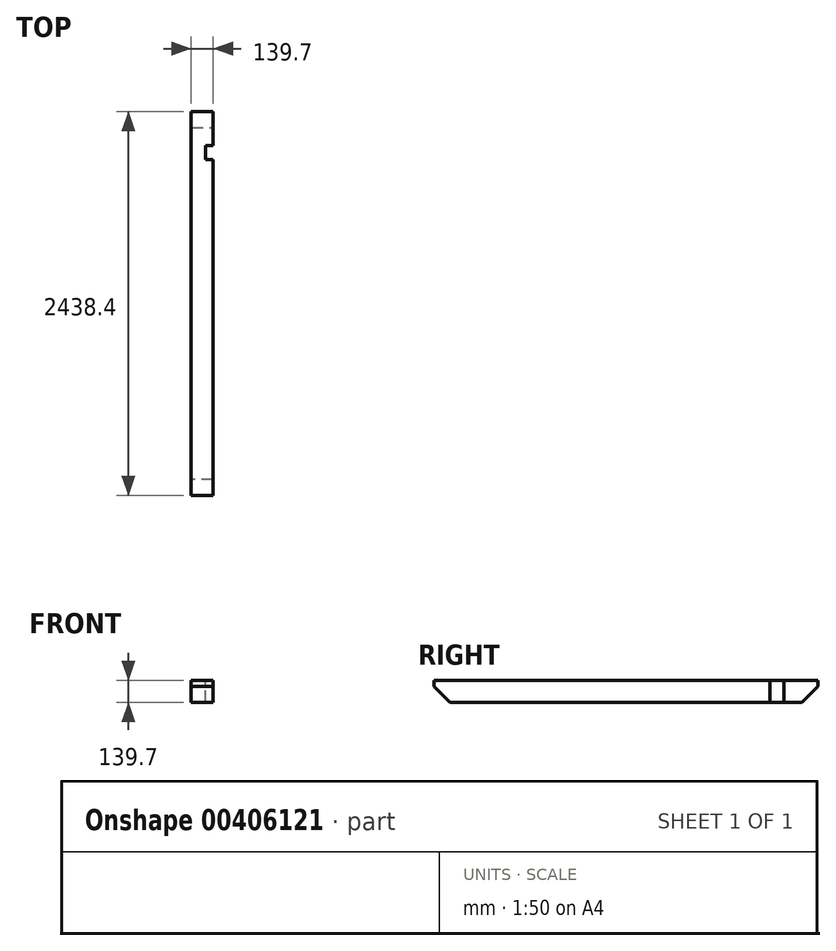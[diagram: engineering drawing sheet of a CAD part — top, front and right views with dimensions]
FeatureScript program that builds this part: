
annotation { "Feature Type Name" : "Feature", "Feature Type Description" : "" }
export const myFeature = defineFeature(function(context is Context, id is Id, definition is map)
    precondition{}
    {
        {
            var Q0;
            Q0=qCreatedBy(makeId("Front.planeOp"),FACE);
            var sketch = newSketch(context, id + "F0", { "sketchPlane" : qUnion([Q0])});
            skLineSegment(sketch, "E0.bottom", {"start": v(69.85, -69.85) * mm, "end": v(-69.85, -69.85) * mm});
            skLineSegment(sketch, "E0.top", {"start": v(69.85, 69.85) * mm, "end": v(-69.85, 69.85) * mm});
            skLineSegment(sketch, "E0.left", {"start": v(69.85, -69.85) * mm, "end": v(69.85, 69.85) * mm});
            skLineSegment(sketch, "E0.right", {"start": v(-69.85, -69.85) * mm, "end": v(-69.85, 69.85) * mm});
            skPoint(sketch, "E0.middle", {"position": v(0, 0) * mm});
            skSolve(sketch);
        }
        {
            var Q0;
            Q0 = qSketchRegion(id + "F0", true);
            extrude(context, id + "F1", {"entities" : qUnion([Q0]), "endBound" : BoundingType.SYMMETRIC, "depth" : 2438.4 * mm});
        }
        {
            var Q0;
            Q0=makeQuery(id+"F1.opExtrude","CAP_EDGE",EDGE,{"disambiguationData":[OSD([sQuery(id+"F0.wireOp",EDGE,"E0.bottom")])],"isStart":false});
            var Q1;
            Q1=makeQuery(id+"F1.opExtrude","CAP_EDGE",EDGE,{"disambiguationData":[OSD([sQuery(id+"F0.wireOp",EDGE,"E0.bottom")])],"isStart":true});
            chamfer(context, id + "F2", {"entities" : qUnion([Q0, Q1]), "width" : 101.6 * mm, "tangentPropagation" : true});
        }
        {
            var Q0;
            Q0=makeQuery(id+"F1.opExtrude","SWEPT_FACE",FACE,{"disambiguationData":[OSD([sQuery(id+"F0.wireOp",EDGE,"E0.left")])]});
            var sketch = newSketch(context, id + "F3", { "sketchPlane" : qUnion([Q0])});
            skLineSegment(sketch, "E1.bottom", {"start": v(1003.3, -69.85) * mm, "end": v(914.4, -69.85) * mm});
            skLineSegment(sketch, "E1.top", {"start": v(1003.3, 69.85) * mm, "end": v(914.4, 69.85) * mm});
            skLineSegment(sketch, "E1.left", {"start": v(1003.3, -69.85) * mm, "end": v(1003.3, 69.85) * mm});
            skLineSegment(sketch, "E1.right", {"start": v(914.4, -69.85) * mm, "end": v(914.4, 69.85) * mm});
            skSolve(sketch);
        }
        {
            var Q0;
            Q0 = qSketchRegion(id + "F3", true);
            extrude(context, id + "F4", {"entities" : qUnion([Q0]), "operationType" : NewBodyOperationType.REMOVE, "depth" : -50.8 * mm});
        }
    });
